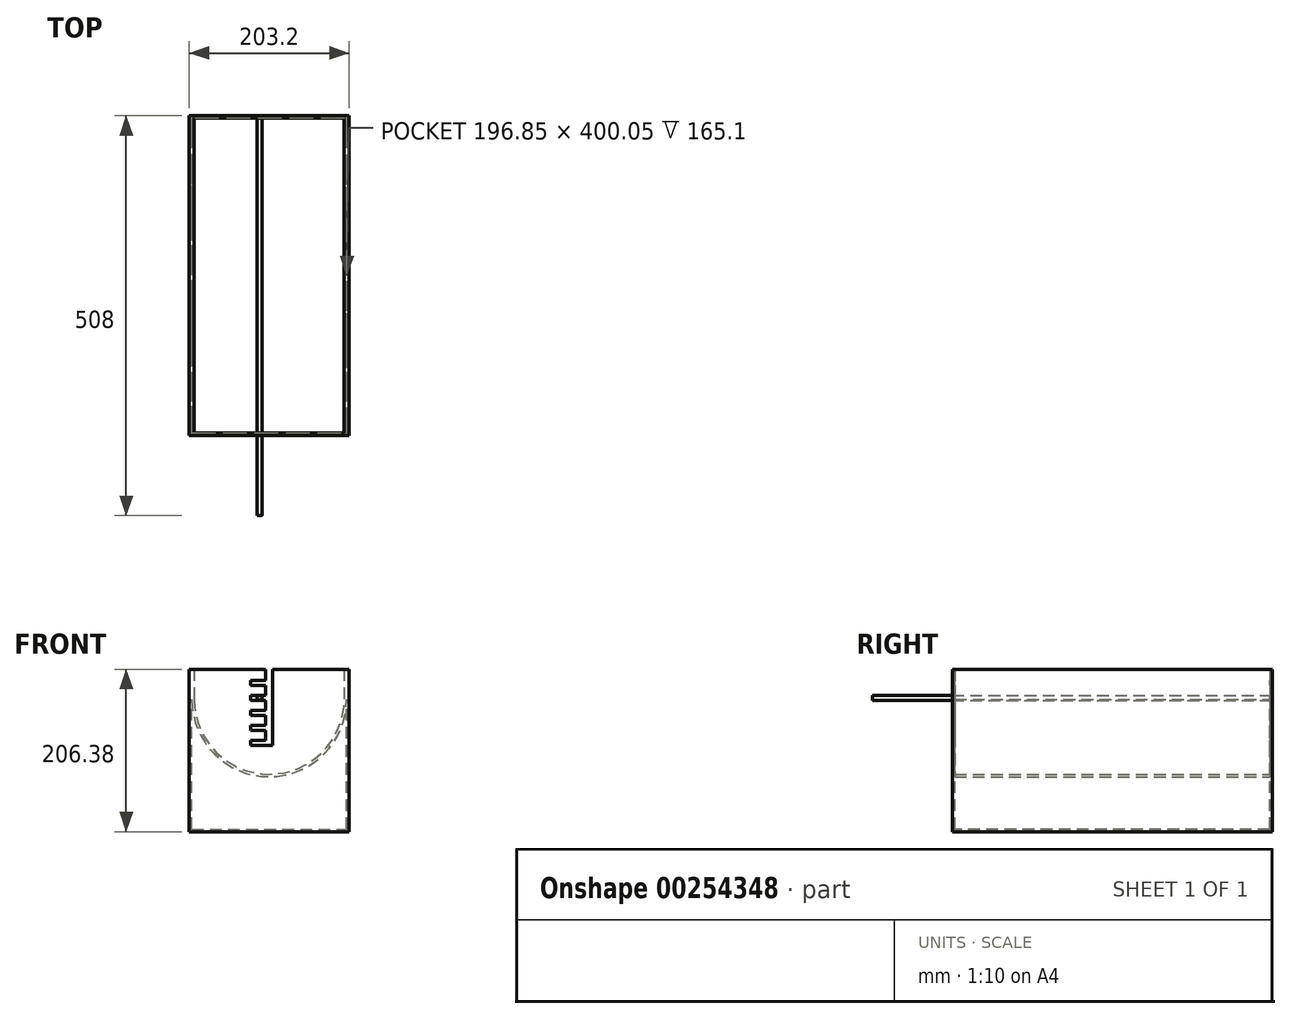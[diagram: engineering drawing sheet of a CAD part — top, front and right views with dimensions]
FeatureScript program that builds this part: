
annotation { "Feature Type Name" : "Feature", "Feature Type Description" : "" }
export const myFeature = defineFeature(function(context is Context, id is Id, definition is map)
    precondition{}
    {
        {
            var Q0;
            Q0=qCreatedBy(makeId("Top.planeOp"),FACE);
            var sketch = newSketch(context, id + "F0", { "sketchPlane" : qUnion([Q0])});
            skLineSegment(sketch, "E0.bottom", {"start": v(101.6, 203.2) * mm, "end": v(-101.6, 203.2) * mm});
            skLineSegment(sketch, "E0.top", {"start": v(101.6, -203.2) * mm, "end": v(-101.6, -203.2) * mm});
            skLineSegment(sketch, "E0.left", {"start": v(101.6, 203.2) * mm, "end": v(101.6, -203.2) * mm});
            skLineSegment(sketch, "E0.right", {"start": v(-101.6, 203.2) * mm, "end": v(-101.6, -203.2) * mm});
            skPoint(sketch, "E0.middle", {"position": v(0, 0) * mm});
            skLineSegment(sketch, "E1.bottom", {"start": v(98.42, 200.03) * mm, "end": v(-98.42, 200.03) * mm});
            skLineSegment(sketch, "E1.top", {"start": v(98.42, -200.03) * mm, "end": v(-98.42, -200.03) * mm});
            skLineSegment(sketch, "E1.left", {"start": v(98.43, 200.03) * mm, "end": v(98.43, -200.03) * mm});
            skLineSegment(sketch, "E1.right", {"start": v(-98.43, 200.03) * mm, "end": v(-98.43, -200.03) * mm});
            skSolve(sketch);
        }
        {
            var Q0;
            Q0 = qSketchRegion(id + "F0", true);
            extrude(context, id + "F1", {"entities" : qUnion([Q0]), "depth" : 203.2 * mm});
        }
        {
            var Q0;
            Q0=makeQuery(id+"F1.opExtrude","SWEPT_FACE",FACE,{"disambiguationData":[OSD([sQuery(id+"F0.wireOp",EDGE,"E0.top")])]});
            var sketch = newSketch(context, id + "F2", { "sketchPlane" : qUnion([Q0])});
            skLineSegment(sketch, "E2.bottom", {"start": v(-101.6, 203.2) * mm, "end": v(101.6, 203.2) * mm});
            skLineSegment(sketch, "E2.top", {"start": v(-101.6, 206.38) * mm, "end": v(101.6, 206.38) * mm});
            skLineSegment(sketch, "E2.left", {"start": v(-101.6, 203.2) * mm, "end": v(-101.6, 206.38) * mm});
            skLineSegment(sketch, "E2.right", {"start": v(101.6, 203.2) * mm, "end": v(101.6, 206.38) * mm});
            skSolve(sketch);
        }
        {
            var Q0;
            Q0 = qSketchRegion(id + "F2", true);
            extrude(context, id + "F3", {"entities" : qUnion([Q0]), "operationType" : NewBodyOperationType.ADD, "oppositeDirection" : true, "depth" : 406.4 * mm});
        }
        {
            var Q0;
            Q0=makeQuery(id+"F3.boolean.opBoolean","MERGE",FACE,{"derivedFrom":[makeQuery(id+"F1.opExtrude","SWEPT_FACE",FACE,{"disambiguationData":[OSD([sQuery(id+"F0.wireOp",EDGE,"E0.bottom")])]}),makeQuery(id+"F3.opExtrude","CAP_FACE",FACE,{"disambiguationData":[OSD([sQuery(id+"F2.wireOp",EDGE,"E2.bottom"),sQuery(id+"F2.wireOp",EDGE,"E2.top"),sQuery(id+"F2.wireOp",EDGE,"E2.left"),sQuery(id+"F2.wireOp",EDGE,"E2.right")])],"isStart":false})]});
            var sketch = newSketch(context, id + "F4", { "sketchPlane" : qUnion([Q0])});
            skLineSegment(sketch, "E3.top", {"start": v(4.38, 0) * mm, "end": v(-4.38, 0) * mm});
            skLineSegment(sketch, "E3.left", {"start": v(4.38, 96.48) * mm, "end": v(4.38, 0) * mm});
            skLineSegment(sketch, "E4.bottom", {"start": v(-4.38, 13.93) * mm, "end": v(-23.43, 13.93) * mm});
            skLineSegment(sketch, "E4.top", {"start": v(-4.38, 20.28) * mm, "end": v(-23.43, 20.28) * mm});
            skLineSegment(sketch, "E4.right", {"start": v(-23.43, 13.93) * mm, "end": v(-23.43, 20.28) * mm});
            skLineSegment(sketch, "E5.0.1.0", {"start": v(-4.38, 39.33) * mm, "end": v(-23.43, 39.33) * mm});
            skLineSegment(sketch, "E5.0.1.1", {"start": v(-4.38, 32.98) * mm, "end": v(-23.43, 32.98) * mm});
            skLineSegment(sketch, "E5.0.1.2", {"start": v(-23.43, 32.98) * mm, "end": v(-23.43, 39.33) * mm});
            skLineSegment(sketch, "E5.0.2.0", {"start": v(-4.38, 58.38) * mm, "end": v(-23.43, 58.38) * mm});
            skLineSegment(sketch, "E5.0.2.1", {"start": v(-4.38, 52.03) * mm, "end": v(-23.43, 52.03) * mm});
            skLineSegment(sketch, "E5.0.2.2", {"start": v(-23.43, 52.03) * mm, "end": v(-23.43, 58.38) * mm});
            skLineSegment(sketch, "E5.0.3.0", {"start": v(-4.38, 77.43) * mm, "end": v(-23.43, 77.43) * mm});
            skLineSegment(sketch, "E5.0.3.1", {"start": v(-4.38, 71.08) * mm, "end": v(-23.43, 71.08) * mm});
            skLineSegment(sketch, "E5.0.3.2", {"start": v(-23.43, 71.08) * mm, "end": v(-23.43, 77.43) * mm});
            skLineSegment(sketch, "E5.0.4.0", {"start": v(-4.38, 96.48) * mm, "end": v(-23.43, 96.48) * mm});
            skLineSegment(sketch, "E5.0.4.1", {"start": v(-4.38, 90.13) * mm, "end": v(-23.43, 90.13) * mm});
            skLineSegment(sketch, "E5.0.4.2", {"start": v(-23.43, 90.13) * mm, "end": v(-23.43, 96.48) * mm});
            skLineSegment(sketch, "E5.direction1", {"start": v(-23.43, 20.28) * mm, "end": v(1.97, 20.28) * mm, "construction": true});
            skLineSegment(sketch, "E5.direction2", {"start": v(-23.43, 20.28) * mm, "end": v(-23.43, 39.33) * mm, "construction": true});
            skLineSegment(sketch, "E6.trimOffspring", {"start": v(-4.38, 90.13) * mm, "end": v(-4.38, 77.43) * mm});
            skLineSegment(sketch, "E7.trimOffspring", {"start": v(-4.38, 71.08) * mm, "end": v(-4.38, 58.38) * mm});
            skLineSegment(sketch, "E8.trimOffspring", {"start": v(-4.38, 52.03) * mm, "end": v(-4.38, 39.33) * mm});
            skLineSegment(sketch, "E9.trimOffspring", {"start": v(-4.38, 32.98) * mm, "end": v(-4.38, 20.28) * mm});
            skLineSegment(sketch, "E10.trimOffspring", {"start": v(-4.38, 13.93) * mm, "end": v(-4.38, 0) * mm});
            skLineSegment(sketch, "E11", {"start": v(-4.38, 96.48) * mm, "end": v(4.38, 96.48) * mm});
            skSolve(sketch);
        }
        {
            var Q0;
            Q0=makeQuery(id+"F4.imprint","IMPRINT",FACE,{"disambiguationData":[TD([[makeQuery(id+"F4.imprint","IMPRINT",EDGE,{"derivedFrom":sQuery(id+"F4.wireOp",EDGE,"E3.bottom")}),1.0]])]});
            var Q1;
            Q1=makeQuery(id+"F4.imprint","IMPRINT",FACE,{"disambiguationData":[TD([[makeQuery(id+"F4.imprint","IMPRINT",EDGE,{"derivedFrom":sQuery(id+"F4.wireOp",EDGE,"E3.top")}),1.0]])]});
            extrude(context, id + "F5", {"entities" : qUnion([Q0, Q1]), "operationType" : NewBodyOperationType.REMOVE, "endBound" : BoundingType.THROUGH_ALL, "oppositeDirection" : true, "depth" : 25.4 * mm});
        }
        {
            var Q0;
            Q0=makeQuery(id+"F1.opExtrude","SWEPT_FACE",FACE,{"disambiguationData":[OSD([sQuery(id+"F0.wireOp",EDGE,"E1.bottom")])]});
            var sketch = newSketch(context, id + "F6", { "sketchPlane" : qUnion([Q0])});
            skLineSegment(sketch, "E12", {"start": v(98.42, 0) * mm, "end": v(98.42, 38.1) * mm});
            skLineSegment(sketch, "E13", {"start": v(-98.42, 0) * mm, "end": v(-98.42, 38.1) * mm});
            skArc(sketch, "E14", {"start": v(98.42, 38.1) * mm, "mid": v(0, 136.53) * mm, "end": v(-98.42, 38.1) * mm});
            skLineSegment(sketch, "E15.0", {"start": v(-95.25, 0) * mm, "end": v(-95.25, 38.1) * mm});
            skArc(sketch, "E15.1", {"start": v(95.25, 38.1) * mm, "mid": v(0, 133.35) * mm, "end": v(-95.25, 38.1) * mm});
            skLineSegment(sketch, "E15.2", {"start": v(95.25, 0) * mm, "end": v(95.25, 38.1) * mm});
            skSolve(sketch);
        }
        {
            var Q0;
            Q0 = qSketchRegion(id + "F6", true);
            var Q1;
            {var subQ2=sQuery(id+"F6.wireOp",EDGE,"E12");Q1=makeQuery(id+"F6.imprint","IMPRINT",FACE,{"disambiguationData":[TD([[makeQuery(id+"F6.imprint","IMPRINT",EDGE,{"derivedFrom":subQ2}),-1.0]])]});}
            var Q2;
            Q2=makeQuery(id+"F1.opExtrude","SWEPT_FACE",FACE,{"disambiguationData":[OSD([sQuery(id+"F0.wireOp",EDGE,"E1.top")])]});
            extrude(context, id + "F7", {"entities" : qUnion([Q0, Q1]), "operationType" : NewBodyOperationType.ADD, "endBound" : BoundingType.UP_TO_SURFACE, "endBoundEntityFace" : qUnion([Q2]), "depth" : 25.4 * mm});
        }
        {
            var Q0;
            Q0=makeQuery(id+"F3.boolean.opBoolean","MERGE",FACE,{"derivedFrom":[makeQuery(id+"F1.opExtrude","SWEPT_FACE",FACE,{"disambiguationData":[OSD([sQuery(id+"F0.wireOp",EDGE,"E0.bottom")])]}),makeQuery(id+"F3.opExtrude","CAP_FACE",FACE,{"disambiguationData":[OSD([sQuery(id+"F2.wireOp",EDGE,"E2.bottom"),sQuery(id+"F2.wireOp",EDGE,"E2.top"),sQuery(id+"F2.wireOp",EDGE,"E2.left"),sQuery(id+"F2.wireOp",EDGE,"E2.right")])],"isStart":false})]});
            var sketch = newSketch(context, id + "F8", { "sketchPlane" : qUnion([Q0])});
            skCircle(sketch, "E16", {"center": v(-12.18, 36.28) * mm, "radius": 3.05 * mm});
            skPoint(sketch, "E16.centerSnap0", {"position": v(-23.43, 36.28) * mm});
            skSolve(sketch);
        }
        {
            var Q0;
            Q0 = qSketchRegion(id + "F8", true);
            var Q1;
            Q1=makeQuery(id+"F3.boolean.opBoolean","MERGE",FACE,{"derivedFrom":[makeQuery(id+"F1.opExtrude","SWEPT_FACE",FACE,{"disambiguationData":[OSD([sQuery(id+"F0.wireOp",EDGE,"E0.top")])]}),makeQuery(id+"F3.opExtrude","CAP_FACE",FACE,{"disambiguationData":[OSD([sQuery(id+"F2.wireOp",EDGE,"E2.bottom"),sQuery(id+"F2.wireOp",EDGE,"E2.top"),sQuery(id+"F2.wireOp",EDGE,"E2.left"),sQuery(id+"F2.wireOp",EDGE,"E2.right")])],"isStart":true})]});
            extrude(context, id + "F9", {"entities" : qUnion([Q0]), "operationType" : NewBodyOperationType.ADD, "oppositeDirection" : true, "endBoundEntityFace" : qUnion([Q1]), "depth" : 508 * mm});
        }
        {
            var Q0;
            Q0=makeQuery(id+"F1.opExtrude","SWEPT_BODY",BODY,{"disambiguationData":[OSD([sQuery(id+"F0.wireOp",EDGE,"E0.bottom"),sQuery(id+"F0.wireOp",EDGE,"E0.top"),sQuery(id+"F0.wireOp",EDGE,"E0.left"),sQuery(id+"F0.wireOp",EDGE,"E0.right"),sQuery(id+"F0.wireOp",EDGE,"E1.bottom"),sQuery(id+"F0.wireOp",EDGE,"E1.top"),sQuery(id+"F0.wireOp",EDGE,"E1.left"),sQuery(id+"F0.wireOp",EDGE,"E1.right")])]});
            var Q1;
            Q1=makeQuery(id+"F9.opExtrude","SWEPT_FACE",FACE,{"disambiguationData":[OSD([sQuery(id+"F8.wireOp",EDGE,"E16")])]});
            transform(context, id + "F10", {"entities" : qUnion([Q0]), "transformType" : TransformType.ROTATION, "transformAxis" : qUnion([Q1]), "angle" : 180 * degree, "makeCopy" : false});
        }
    });
